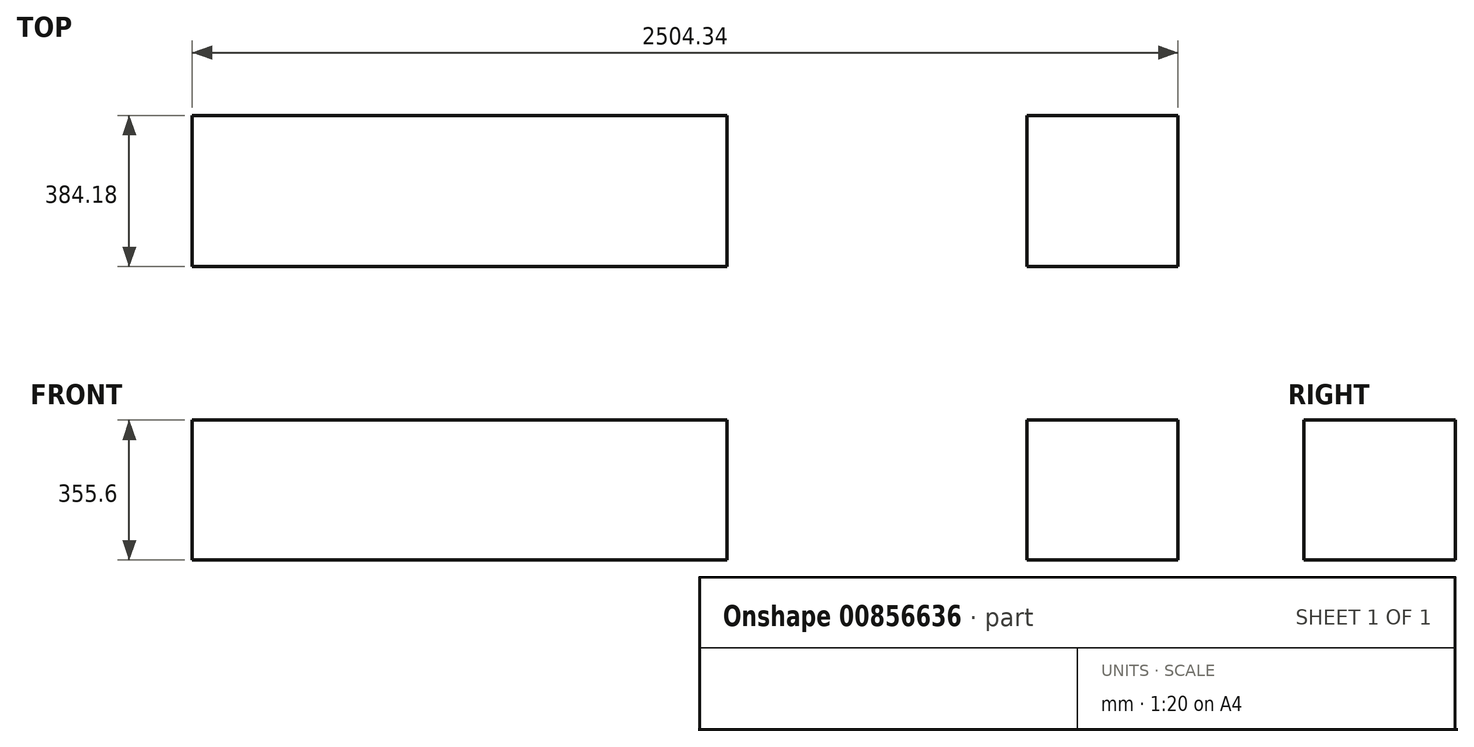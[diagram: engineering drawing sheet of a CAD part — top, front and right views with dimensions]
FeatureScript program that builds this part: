
annotation { "Feature Type Name" : "Feature", "Feature Type Description" : "" }
export const myFeature = defineFeature(function(context is Context, id is Id, definition is map)
    precondition{}
    {
        {
            var Q0;
            Q0=qCreatedBy(makeId("Front.planeOp"),FACE);
            var sketch = newSketch(context, id + "F0", { "sketchPlane" : qUnion([Q0])});
            skLineSegment(sketch, "E0.bottom", {"start": v(1208.67, 0) * mm, "end": v(2113.54, 0) * mm});
            skLineSegment(sketch, "E0.top", {"start": v(1208.67, 1778) * mm, "end": v(2113.54, 1778) * mm});
            skLineSegment(sketch, "E0.left", {"start": v(1208.67, 0) * mm, "end": v(1208.67, 1778) * mm});
            skLineSegment(sketch, "E0.right", {"start": v(2113.54, 0) * mm, "end": v(2113.54, 1778) * mm});
            skLineSegment(sketch, "E1.left", {"start": v(0, 0) * mm, "end": v(0.1, 863.6) * mm});
            skLineSegment(sketch, "E1.right", {"start": v(-1905, -2.15) * mm, "end": v(-1904.9, 861.45) * mm});
            skLineSegment(sketch, "E2.top", {"start": v(0.1, 901.7) * mm, "end": v(-2504.34, 901.7) * mm});
            skLineSegment(sketch, "E2.left", {"start": v(0.1, 863.6) * mm, "end": v(0.1, 901.7) * mm});
            skLineSegment(sketch, "E2.right", {"start": v(-2504.34, 863.6) * mm, "end": v(-2504.34, 901.7) * mm});
            skLineSegment(sketch, "E3", {"start": v(-1904.9, 1058.57) * mm, "end": v(-1904.9, -228.77) * mm, "construction": true});
            skLineSegment(sketch, "E4", {"start": v(0, 1058.57) * mm, "end": v(0, -228.77) * mm, "construction": true});
            skLineSegment(sketch, "E5.bottom", {"start": v(0, 0) * mm, "end": v(-381, 0) * mm});
            skLineSegment(sketch, "E5.left", {"start": v(0, 0) * mm, "end": v(0, 857.25) * mm});
            skLineSegment(sketch, "E6", {"start": v(-381, 0) * mm, "end": v(-387.35, 0) * mm, "construction": true});
            skLineSegment(sketch, "E7.bottom", {"start": v(-387.35, 0) * mm, "end": v(-1143, 0) * mm, "construction": true});
            skLineSegment(sketch, "E7.left", {"start": v(-387.35, 0) * mm, "end": v(-387.35, 736.6) * mm, "construction": true});
            skLineSegment(sketch, "E8", {"start": v(0, 0) * mm, "end": v(-1905, -2.15) * mm, "construction": true});
            skLineSegment(sketch, "E9.bottom", {"start": v(-387.35, 857.25) * mm, "end": v(-1143, 857.25) * mm, "construction": true});
            skLineSegment(sketch, "E9.top", {"start": v(-387.35, 121.5) * mm, "end": v(-1143, 120.65) * mm, "construction": true});
            skLineSegment(sketch, "E9.left", {"start": v(-387.35, 857.25) * mm, "end": v(-387.35, 121.5) * mm, "construction": true});
            skLineSegment(sketch, "E9.right", {"start": v(-1143, 857.25) * mm, "end": v(-1143, 120.65) * mm, "construction": true});
            skLineSegment(sketch, "E10", {"start": v(-1149.35, 857.25) * mm, "end": v(-1149.35, 120.65) * mm, "construction": true});
            skLineSegment(sketch, "E11.bottom", {"start": v(-1149.35, 857.25) * mm, "end": v(-1527.18, 857.25) * mm});
            skLineSegment(sketch, "E11.top", {"start": v(-1149.35, 82.55) * mm, "end": v(-1527.18, 82.55) * mm});
            skLineSegment(sketch, "E11.left", {"start": v(-1149.35, 857.25) * mm, "end": v(-1149.35, 82.55) * mm});
            skLineSegment(sketch, "E11.right", {"start": v(-1527.18, 857.25) * mm, "end": v(-1527.18, 82.55) * mm});
            skLineSegment(sketch, "E12", {"start": v(-1527.18, 82.55) * mm, "end": v(-1533.53, 82.54) * mm, "construction": true});
            skLineSegment(sketch, "E13.bottom", {"start": v(-1533.53, 82.54) * mm, "end": v(-1911.35, 82.54) * mm});
            skLineSegment(sketch, "E13.top", {"start": v(-1533.53, 857.25) * mm, "end": v(-1911.35, 857.25) * mm});
            skLineSegment(sketch, "E13.left", {"start": v(-1533.53, 82.54) * mm, "end": v(-1533.53, 857.25) * mm});
            skLineSegment(sketch, "E13.right", {"start": v(-1911.35, 82.54) * mm, "end": v(-1911.35, 857.25) * mm});
            skLineSegment(sketch, "E14", {"start": v(0, 857.25) * mm, "end": v(-2682.58, 857.25) * mm, "construction": true});
            skLineSegment(sketch, "E15.bottom", {"start": v(0, 857.25) * mm, "end": v(-381, 857.25) * mm});
            skLineSegment(sketch, "E15.top", {"start": v(0, 82.55) * mm, "end": v(-381, 82.55) * mm});
            skLineSegment(sketch, "E15.left", {"start": v(0, 857.25) * mm, "end": v(0, 82.55) * mm});
            skLineSegment(sketch, "E15.right", {"start": v(-381, 857.25) * mm, "end": v(-381, 82.55) * mm});
            skLineSegment(sketch, "E16.bottom", {"start": v(-387.35, 82.55) * mm, "end": v(-1143, 82.55) * mm});
            skLineSegment(sketch, "E16.top", {"start": v(-387.35, 115.22) * mm, "end": v(-1143, 115.22) * mm});
            skLineSegment(sketch, "E16.left", {"start": v(-387.35, 82.55) * mm, "end": v(-387.35, 115.22) * mm});
            skLineSegment(sketch, "E16.right", {"start": v(-1143, 82.55) * mm, "end": v(-1143, 115.22) * mm});
            skPoint(sketch, "E17", {"position": v(-765.18, 121.08) * mm});
            skPoint(sketch, "E18", {"position": v(-1530.35, 82.55) * mm});
            skPoint(sketch, "E18.positionSnap0", {"position": v(-1530.35, 82.55) * mm});
            skLineSegment(sketch, "E19.bottom", {"start": v(0, 0) * mm, "end": v(-3447.41, 0) * mm});
            skLineSegment(sketch, "E19.top", {"start": v(0, 2438.4) * mm, "end": v(-384.18, 2438.4) * mm});
            skLineSegment(sketch, "E19.left", {"start": v(0, 0) * mm, "end": v(0, 1524) * mm});
            skLineSegment(sketch, "E19.right", {"start": v(-3447.41, 0) * mm, "end": v(-3447.42, 2438.4) * mm});
            skLineSegment(sketch, "E20.bottom", {"start": v(-2504.34, 0) * mm, "end": v(-2542.44, 0) * mm});
            skLineSegment(sketch, "E20.left", {"start": v(-2504.34, 0) * mm, "end": v(-2504.34, 1549.4) * mm});
            skLineSegment(sketch, "E20.right", {"start": v(-2542.44, 0) * mm, "end": v(-2542.44, 2438.4) * mm});
            skLineSegment(sketch, "E21", {"start": v(-3447.31, 2438.4) * mm, "end": v(-3447.31, 0) * mm, "construction": true});
            skLineSegment(sketch, "E22.bottom", {"start": v(-3447.31, 2438.4) * mm, "end": v(-3485.52, 2438.4) * mm});
            skLineSegment(sketch, "E22.top", {"start": v(-3447.31, 0) * mm, "end": v(-3485.51, 0) * mm});
            skLineSegment(sketch, "E22.left", {"start": v(-3447.31, 2438.4) * mm, "end": v(-3447.31, 0) * mm});
            skLineSegment(sketch, "E22.right", {"start": v(-3485.52, 2438.4) * mm, "end": v(-3485.51, 0) * mm});
            skLineSegment(sketch, "E23", {"start": v(-3447.31, 1778) * mm, "end": v(-2542.44, 1778) * mm});
            skLineSegment(sketch, "E24", {"start": v(-765.18, 121.08) * mm, "end": v(-765.18, 1778) * mm, "construction": true});
            skPoint(sketch, "E25.middle", {"position": v(-765.18, 1778) * mm});
            skLineSegment(sketch, "E26.bottom", {"start": v(-2504.34, 2133.6) * mm, "end": v(-1146.18, 2133.6) * mm});
            skLineSegment(sketch, "E26.top", {"start": v(-2504.34, 1778) * mm, "end": v(-1146.18, 1778) * mm});
            skLineSegment(sketch, "E26.left", {"start": v(-2504.34, 2438.4) * mm, "end": v(-2504.34, 1778) * mm});
            skLineSegment(sketch, "E26.right", {"start": v(-1146.18, 2133.6) * mm, "end": v(-1146.18, 1955.8) * mm});
            skLineSegment(sketch, "E27.bottom", {"start": v(0, 2133.58) * mm, "end": v(-384.18, 2133.58) * mm});
            skLineSegment(sketch, "E27.top", {"start": v(0, 1778) * mm, "end": v(-384.18, 1778) * mm});
            skLineSegment(sketch, "E27.left", {"start": v(0, 2133.58) * mm, "end": v(0, 1778) * mm});
            skLineSegment(sketch, "E27.right", {"start": v(-384.18, 2133.58) * mm, "end": v(-384.18, 1778) * mm});
            skLineSegment(sketch, "E28.left", {"start": v(-1146.18, 2438.4) * mm, "end": v(-1146.18, 1778) * mm});
            skLineSegment(sketch, "E28.right", {"start": v(-384.18, 2438.4) * mm, "end": v(-384.18, 1955.8) * mm});
            skLineSegment(sketch, "E29.top", {"start": v(-2504.34, 1524) * mm, "end": v(-1146.18, 1524) * mm});
            skLineSegment(sketch, "E29.left", {"start": v(-2504.34, 1549.4) * mm, "end": v(-2504.34, 1524) * mm});
            skLineSegment(sketch, "E30.bottom", {"start": v(-384.18, 1778) * mm, "end": v(0, 1778) * mm});
            skLineSegment(sketch, "E31.1", {"start": v(-2504.34, 1549.4) * mm, "end": v(-1171.58, 1549.4) * mm});
            skLineSegment(sketch, "E32.trimOffspring", {"start": v(-2504.34, 1778) * mm, "end": v(-2504.34, 2438.4) * mm});
            skLineSegment(sketch, "E33.trimOffspring", {"start": v(-2542.44, 2438.4) * mm, "end": v(-3447.42, 2438.4) * mm});
            skPoint(sketch, "E25.bottom.start.orphan", {"position": v(-384.18, 2438.4) * mm});
            skLineSegment(sketch, "E34.trimOffspring", {"start": v(-1146.18, 2438.4) * mm, "end": v(-2504.34, 2438.4) * mm});
            skPoint(sketch, "E30.right.end.orphan", {"position": v(0, 1524) * mm});
            skLineSegment(sketch, "E35.trimOffspring", {"start": v(0, 1778) * mm, "end": v(0, 2438.4) * mm});
            skSolve(sketch);
        }
        {
            var Q0;
            {var subQ2=sQuery(id+"F0.wireOp",EDGE,"E26.bottom");Q0=makeQuery(id+"F0.imprint","IMPRINT",FACE,{"disambiguationData":[TD([[makeQuery(id+"F0.imprint","IMPRINT",EDGE,{"derivedFrom":subQ2}),-1.0]])]});}
            var Q1;
            {var subQ3=sQuery(id+"F0.wireOp",EDGE,"E27.bottom");Q1=makeQuery(id+"F0.imprint","IMPRINT",FACE,{"disambiguationData":[TD([[makeQuery(id+"F0.imprint","IMPRINT",EDGE,{"derivedFrom":subQ3}),1.0]])]});}
            extrude(context, id + "F1", {"entities" : qUnion([Q0, Q1]), "oppositeDirection" : true, "depth" : 609.6 * mm, "offsetDistance" : 25.4 * mm, "hasSecondDirection" : true, "secondDirectionOppositeDirection" : true, "secondDirectionDepth" : 225.42 * mm});
        }
    });
